# Revit family: Doors_Openers_DITEC_DAB305_1 Arm system PUSH
name_source: partatom
category: Doors
units: mm (PartAtom-declared; Revit-internal decimal feet)

## family parameters
Always vertical = Yes
Cut with Voids When Loaded = No
Host = Wall
OmniClass Number = 23.30.10.00
OmniClass Title = Doors
Room Calculation Point = No
Shared = No

## types (1)
- Doors_Openers_DITEC_DAB305_1 Arm system PUSH
    Analytic Construction = <None>
    Define Thermal Properties by = Schematic Type
    Door Frame Material = Ditec-Anodized Aluminium
    Door Glass Material = Ditec-Glass Clear
    Function = Interior
    Height = 2100 mm
    Model = DAB305
    Technical Manual = https://www.ditecautomations.com
    Wall Closure = By host
    Width = 1100 mm  [stored 3.60892 ft]

note: [stored X ft] marks values corroborated as IEEE doubles in the binary element streams (Revit-internal decimal feet)

## geometry (parser evidence)
native form markers: Blend x8, Sweep x41
no freeform markers — native parametric forms only
